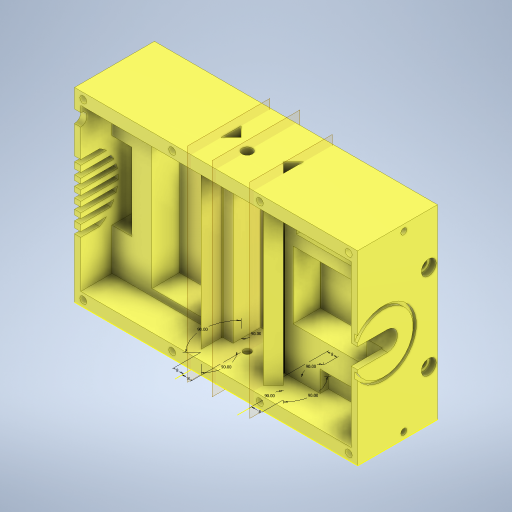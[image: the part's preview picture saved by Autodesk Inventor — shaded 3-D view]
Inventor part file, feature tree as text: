
AUTODESK INVENTOR PART (.ipt)
format: ipt  version: 2023 (Build 270158030, 158C)  size: 804,864 bytes
history: native  units: mm
features: sketch x19, extrude x18, projected_geometry x7, hole x6, plane x4, mirror x2
ambient origin geometry x8: Origin, YZ Plane, XZ Plane, XY Plane, X Axis, Y Axis, Z Axis, Center Point
bodies: Solid1 (feature_tree)
feature tree (56):
  extrude  "MainInnerBodyExtrusion"  Depth=149.0mm
  extrude  "HoleForCamerabase"  Depth=50.0mm
  extrude  "HoleForFan"  Depth=59.0mm
  extrude  "HoleForPi"  TaperAngle=0.0deg  [1 undecoded]
  extrude  "HoleForPoeAdapter"  Depth=62.0mm
  extrude  "HoleForThermister"  Depth=47.0mm
  extrude  "HoleForSensor"  Depth=32.0mm
  extrude  "SlotsForRearFan"  Depth=47.0mm
  extrude  "VentForCamera"  Depth=16.0mm
  extrude  "HoleForLens"  Depth=118.0mm
  sketch  "Sketch23"  dims[d26=49.0mm d27=118.0mm]
  hole  "Hole for 6-32 Insert"  [1 undecoded]
  hole  "Screw hole for 6-32 screw"  [1 undecoded]
  hole  "Side hole for 1-4 20 insert"  [1 undecoded]
  mirror  "Mirror for side insert"
  extrude  "Extrusion18"  Depth=17.0mm
  extrude  "HoleForPowerWire"  TaperAngle=0.0deg  [1 undecoded]
  extrude  "Extrusion22"  Depth=2.0mm
  extrude  "Extrusion23"  Depth=4.0mm
  extrude  "ExtrusionForBottom"  Depth=4.0mm
  hole  "1-4 holesToBoltFixture"  [1 undecoded]
  plane  "Work Plane1"
  plane  "Work Plane2"
  mirror  "Mirror4"
  extrude  "CutOutForFilter"  Depth=22.0mm
  hole  "Hole13"  [1 undecoded]
  plane  "Work Plane4"
  plane  "Work Plane5"
  hole  "Hole15"  [1 undecoded]
  extrude  "Extrusion35"  Depth=10.0mm
  extrude  "Extrusion36"  Depth=16.0mm
  sketch  "Sketch1"  dims[d0=222.7mm d1=149.0mm]
  sketch  "Sketch3"  dims[d2=50.0mm d3=0.0mm d5=15.7mm]
  sketch  "Sketch4"  dims[d6=54.0mm d7=59.0mm]
  sketch  "Sketch6"  dims[d8=47.0mm d9=0.0mm]
  sketch  "Sketch7"  dims[d13=16.0mm d14=62.0mm]
  sketch  "Sketch11"  dims[d15=3.0mm d16=47.0mm]
  sketch  "Sketch15"  dims[d17=0.0mm d20=32.0mm]
  sketch  "Sketch16"  dims[d21=129.0mm d22=47.0mm]
  sketch  "Sketch18"  dims[d23=0.0mm d25=16.0mm]
  sketch  "Sketch24"  dims[d28=47.0mm d29=0.0mm]
  sketch  "Sketch25"  dims[d36=69.0mm d37=28.0mm]
  projected_geometry  "Projected Loop1"
  sketch  "Sketch26"  dims[d38=47.0mm d39=0.0mm]
  sketch  "Sketch37"  dims[d42=50.0mm d43=17.0mm]
  projected_geometry  "Projected Loop3"
  projected_geometry  "Projected Loop4"
  sketch  "Sketch39"  dims[d46=31.5mm d47=0.0mm]
  projected_geometry  "Projected Loop5"
  sketch  "Sketch40"  dims[d67=60.0mm d69=2.0mm]
  sketch  "Sketch43"  dims[d71=4.0mm d72=4.0mm]
  projected_geometry  "Projected Loop8"
  projected_geometry  "Projected Loop11"
  sketch  "Sketch47"  dims[d73=4.0mm d75=4.0mm]
  projected_geometry  "Projected Loop12"
  sketch  "Sketch50"  dims[d76=10.0mm d77=0.0mm d78=15.5mm d79=22.0mm d85=3.0mm d86=3.0mm d87=10.0mm d88=16.0mm d89=1.5mm d90=3.0mm d91=3.0mm d92=3.0mm d93=0.0mm d94=0.0mm d95=15.0mm d97=16.0mm d98=10.0mm d99=0.0mm d106=5.0mm d108=5.0mm d109=4.7mm d110=6.0mm d111=5.54mm d112=5.55mm d113=90.0deg d114=7.2mm d115=20.594885mm d116=3.797mm d117=6.0mm d118=12.7mm d119=2.362mm d120=90.0deg d121=15.0mm d122=20.594885mm d130=7.666mm d131=6.0mm d132=8.406mm d133=7.41mm d134=90.0deg d135=9.53mm d136=20.594885mm d137=24.0mm d138=10.0mm d139=3.0mm d140=25.0mm d141=0.0mm d142=30.0mm d144=10.0mm d145=0.0mm d222=76.2mm d223=76.2mm d224=76.2mm d225=76.2mm d226=25.0mm d227=111.350057mm d228=2.0mm d229=0.0mm d230=2.0mm d231=0.0mm d232=14.0mm d233=0.0mm d234=7.0mm d235=40.0mm d236=40.0mm d237=7.142mm d238=6.0mm d239=12.0mm d240=5.0mm d241=90.0deg d242=135.0mm d243=20.594885mm d246=30.0mm d247=-20.0mm d255=21.0mm d256=52.25mm d257=47.0mm d258=2.25mm d259=0.0mm d264=90.0deg d265=90.0deg d266=90.0deg d267=8.0mm d268=8.0mm d269=8.0mm d270=8.0mm d271=90.0deg d272=90.0deg d273=90.0deg d293=27.0mm d294=5.0mm d295=5.0mm d296=4.699mm d297=6.0mm d298=4.8514mm d299=5.55244mm d300=90.0deg d301=7.1374mm d302=0.0mm d314=8.0mm d315=6.0mm d316=9.52mm d317=9.9mm d318=90.0deg d319=12.75mm d320=0.0mm d325=149.0mm d326=0.0mm d327=149.0mm d328=0.0mm]
note: 8 required parameter values undecoded (feature->parameter linkage not recoverable at this tier; creation-order binding heuristic only, values carry confidence <= 0.55)
